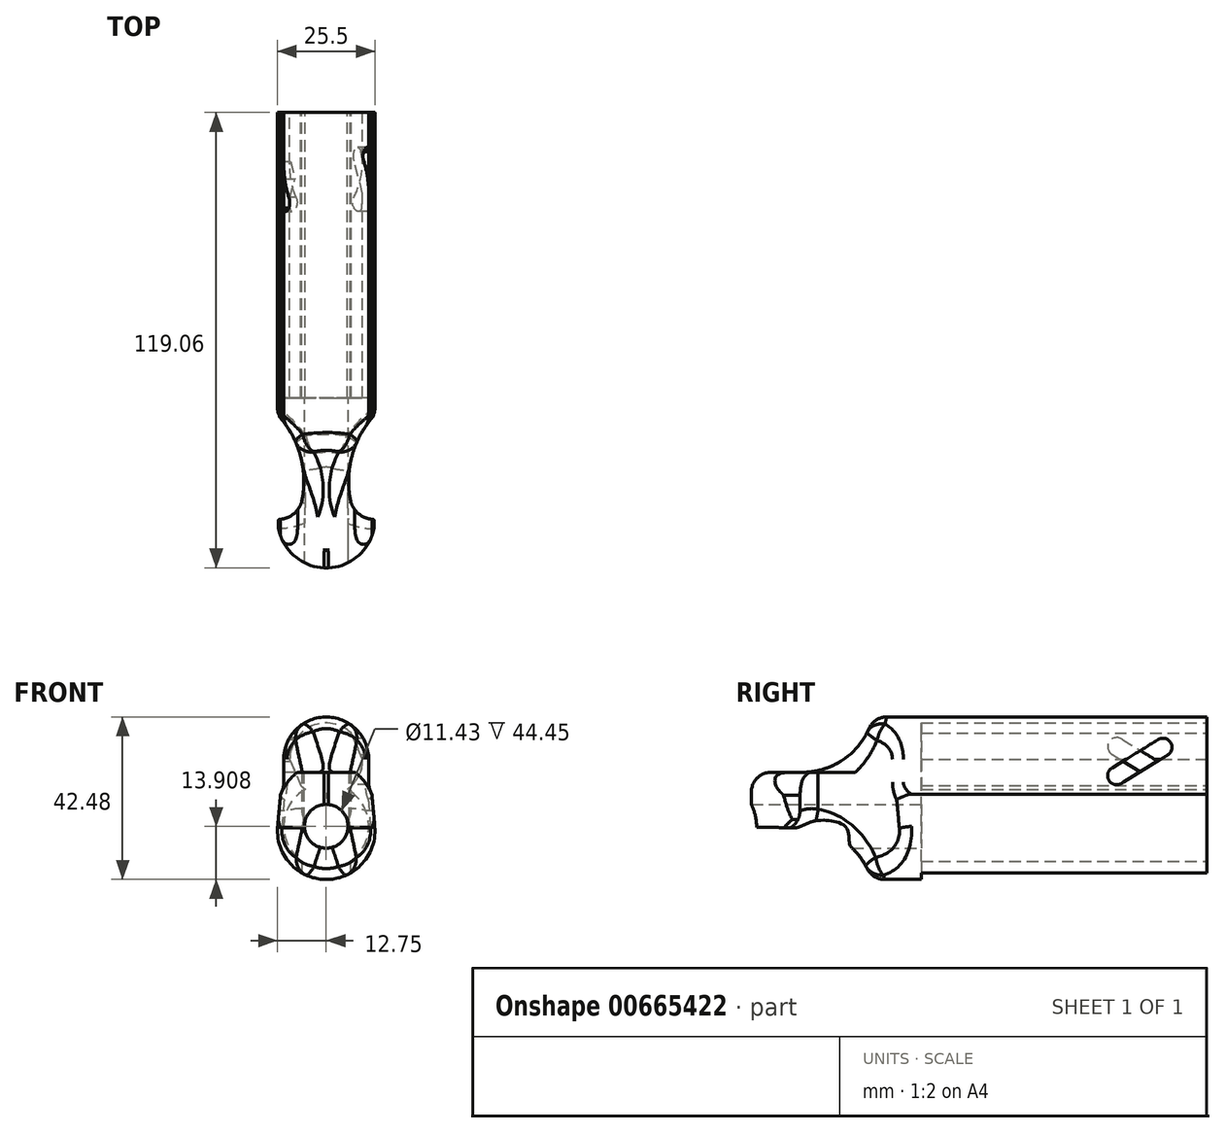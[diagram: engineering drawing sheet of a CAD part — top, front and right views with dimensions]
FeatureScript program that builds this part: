
annotation { "Feature Type Name" : "Feature", "Feature Type Description" : "" }
export const myFeature = defineFeature(function(context is Context, id is Id, definition is map)
    precondition{}
    {
        {
            var Q0;
            Q0=qCreatedBy(makeId("Front.planeOp"),FACE);
            var sketch = newSketch(context, id + "F0", { "sketchPlane" : qUnion([Q0])});
            skArc(sketch, "E0", {"start": v(5.48, -7.8) * mm, "mid": v(0, 9.53) * mm, "end": v(-5.48, -7.8) * mm});
            skArc(sketch, "E1", {"start": v(-5.48, -7.8) * mm, "mid": v(0, -28.58) * mm, "end": v(5.48, -7.8) * mm});
            skArc(sketch, "E2", {"start": v(11.11, 0) * mm, "mid": v(0, 11.11) * mm, "end": v(-11.11, 0) * mm});
            skLineSegment(sketch, "E3", {"start": v(11.11, 0) * mm, "end": v(12.7, -17.46) * mm});
            skLineSegment(sketch, "E4", {"start": v(-11.11, 0) * mm, "end": v(-12.7, -17.46) * mm});
            skLineSegment(sketch, "E5", {"start": v(17.46, -12.3) * mm, "end": v(37.37, -12.3) * mm});
            skLineSegment(sketch, "E6", {"start": v(11.11, 24.47) * mm, "end": v(37.37, -12.3) * mm});
            skLineSegment(sketch, "E7", {"start": v(11.11, -5.95) * mm, "end": v(11.11, 24.47) * mm});
            skPoint(sketch, "E8.visualSharp", {"position": v(11.11, -12.3) * mm});
            skArc(sketch, "E8.filletArc", {"start": v(11.11, -5.95) * mm, "mid": v(12.97, -10.44) * mm, "end": v(17.46, -12.3) * mm});
            skLineSegment(sketch, "E9.MirrorCS", {"start": v(-11.11, 24.47) * mm, "end": v(-37.37, -12.3) * mm});
            skLineSegment(sketch, "E10.MirrorCS", {"start": v(-11.11, -5.95) * mm, "end": v(-11.11, 24.47) * mm});
            skArc(sketch, "E11.MirrorCS", {"start": v(-11.11, -5.95) * mm, "mid": v(-12.97, -10.44) * mm, "end": v(-17.46, -12.3) * mm});
            skLineSegment(sketch, "E12.MirrorCS", {"start": v(-17.46, -12.3) * mm, "end": v(-37.37, -12.3) * mm});
            skArc(sketch, "E13", {"start": v(-12.7, -17.46) * mm, "mid": v(0, -31.37) * mm, "end": v(12.7, -17.46) * mm});
            skSolve(sketch);
        }
        {
            var Q0;
            {var subQ0=sQuery(id+"F0.wireOp",EDGE,"E0");Q0=makeQuery(id+"F0.imprint","IMPRINT",FACE,{"disambiguationData":[TD([[makeQuery(id+"F0.imprint","IMPRINT",EDGE,{"derivedFrom":subQ0}),-1.0]])]});}
            extrude(context, id + "F1", {"entities" : qUnion([Q0]), "depth" : 74.61 * mm, "offsetDistance" : 25.4 * mm});
        }
        {
            var Q0;
            Q0=makeQuery(id+"F1.opExtrude","CAP_FACE",FACE,{"disambiguationData":[OSD([sQuery(id+"F0.wireOp",EDGE,"E0"),sQuery(id+"F0.wireOp",EDGE,"E1"),sQuery(id+"F0.wireOp",EDGE,"i93pHt0q-3cz8-Kv8p-NXo6-p6uIZiVqrdmw"),sQuery(id+"F0.wireOp",EDGE,"D1jruoxV-a4U2-s1l0-eM7a-wT1BJkcVVtK3"),sQuery(id+"F0.wireOp",EDGE,"qe1SkhRB-ESz2-ejrM-H6ui-Tdr1pgu2zREs"),sQuery(id+"F0.wireOp",EDGE,"50cb2b35-ebb8-4a2a-ac11-31013a324220.filletArc"),sQuery(id+"F0.wireOp",EDGE,"ced6b576-02da-43b8-b345-90776f59c21b.filletArc"),sQuery(id+"F0.wireOp",EDGE,"7c9acb4f-49cb-4d03-afd4-daee15c41fa80.MirrorCS"),sQuery(id+"F0.wireOp",EDGE,"7c9acb4f-49cb-4d03-afd4-daee15c41fa81.MirrorCS"),sQuery(id+"F0.wireOp",EDGE,"7c9acb4f-49cb-4d03-afd4-daee15c41fa82.MirrorCS"),sQuery(id+"F0.wireOp",EDGE,"7c9acb4f-49cb-4d03-afd4-daee15c41fa83.MirrorCS"),sQuery(id+"F0.wireOp",EDGE,"7c9acb4f-49cb-4d03-afd4-daee15c41fa84.MirrorCS")])],"isStart":false});
            var sketch = newSketch(context, id + "F2", { "sketchPlane" : qUnion([Q0])});
            skArc(sketch, "E14", {"start": v(11.11, -5.95) * mm, "mid": v(11.32, -7.57) * mm, "end": v(11.94, -9.08) * mm});
            skArc(sketch, "E15", {"start": v(-11.94, -9.08) * mm, "mid": v(-11.32, -7.57) * mm, "end": v(-11.11, -5.95) * mm});
            skArc(sketch, "E16", {"start": v(-12.7, -17.46) * mm, "mid": v(0, -31.37) * mm, "end": v(12.7, -17.46) * mm});
            skArc(sketch, "E17", {"start": v(11.11, 0) * mm, "mid": v(0, 11.11) * mm, "end": v(-11.11, 0) * mm});
            skLineSegment(sketch, "E18", {"start": v(-11.11, 0) * mm, "end": v(-11.11, -5.95) * mm});
            skLineSegment(sketch, "E19", {"start": v(11.11, 0) * mm, "end": v(11.11, -5.95) * mm});
            skLineSegment(sketch, "E20", {"start": v(11.94, -9.08) * mm, "end": v(12.7, -17.46) * mm});
            skLineSegment(sketch, "E21", {"start": v(-11.94, -9.08) * mm, "end": v(-12.7, -17.46) * mm});
            skSolve(sketch);
        }
        {
            var Q0;
            Q0=qCreatedBy(makeId("Front.planeOp"),FACE);
            var sketch = newSketch(context, id + "F3", { "sketchPlane" : qUnion([Q0])});
            skLineSegment(sketch, "E22.bottom", {"start": v(-6.35, -36.2) * mm, "end": v(6.35, -36.2) * mm});
            skLineSegment(sketch, "E22.top", {"start": v(-6.35, -26.33) * mm, "end": v(6.35, -26.33) * mm});
            skLineSegment(sketch, "E22.left", {"start": v(-6.35, -36.2) * mm, "end": v(-6.35, -26.33) * mm});
            skLineSegment(sketch, "E22.right", {"start": v(6.35, -36.2) * mm, "end": v(6.35, -26.33) * mm});
            skPoint(sketch, "E22.middle", {"position": v(0, -31.27) * mm});
            skSolve(sketch);
        }
        {
            var Q0;
            Q0=makeQuery(id+"F3.imprint","IMPRINT",FACE,{"disambiguationData":[TD([[makeQuery(id+"F3.imprint","IMPRINT",EDGE,{"derivedFrom":sQuery(id+"F3.wireOp",EDGE,"E22.bottom")}),1.0]])]});
            extrude(context, id + "F4", {"entities" : qUnion([Q0]), "operationType" : NewBodyOperationType.REMOVE, "depth" : 75.44 * mm, "offsetDistance" : 25.4 * mm});
        }
        {
            var Q0;
            Q0 = qSketchRegion(id + "F2", true);
            extrude(context, id + "F5", {"entities" : qUnion([Q0]), "operationType" : NewBodyOperationType.ADD, "depth" : 6.35 * mm, "offsetDistance" : 25.4 * mm});
        }
        {
            var Q0;
            Q0=makeQuery(id+"F5.opExtrude","CAP_FACE",FACE,{"disambiguationData":[OSD([sQuery(id+"F2.wireOp",EDGE,"E14"),sQuery(id+"F2.wireOp",EDGE,"E15"),sQuery(id+"F2.wireOp",EDGE,"E16"),sQuery(id+"F2.wireOp",EDGE,"E17"),sQuery(id+"F2.wireOp",EDGE,"E18"),sQuery(id+"F2.wireOp",EDGE,"E19"),sQuery(id+"F2.wireOp",EDGE,"E20"),sQuery(id+"F2.wireOp",EDGE,"E21")])],"isStart":false});
            cPlane(context, id + "F6", {"entities" : qUnion([Q0]), "cplaneType" : CPlaneType.OFFSET, "offset" : 0 * mm, "width" : 152.4 * mm, "height" : 152.4 * mm});
        }
        {
            var Q0;
            Q0=qCreatedBy(id+"F6.planeOp",FACE);
            var sketch = newSketch(context, id + "F7", { "sketchPlane" : qUnion([Q0])});
            skArc(sketch, "E23", {"start": v(11.11, 0) * mm, "mid": v(0, 11.11) * mm, "end": v(-11.11, 0) * mm});
            skSolve(sketch);
        }
        {
            var Q0;
            Q0=qCreatedBy(id+"F6.planeOp",FACE);
            var sketch = newSketch(context, id + "F8", { "sketchPlane" : qUnion([Q0])});
            skArc(sketch, "E24", {"start": v(-12.7, -17.46) * mm, "mid": v(0, -31.37) * mm, "end": v(12.7, -17.46) * mm});
            skLineSegment(sketch, "E25", {"start": v(-11.11, 0) * mm, "end": v(-11.11, -5.95) * mm});
            skLineSegment(sketch, "E26", {"start": v(11.11, 0) * mm, "end": v(11.11, -5.95) * mm});
            skArc(sketch, "E27", {"start": v(11.11, -5.95) * mm, "mid": v(11.32, -7.57) * mm, "end": v(11.94, -9.08) * mm});
            skLineSegment(sketch, "E28", {"start": v(11.94, -9.08) * mm, "end": v(12.7, -17.46) * mm});
            skArc(sketch, "E29", {"start": v(-11.94, -9.08) * mm, "mid": v(-11.32, -7.57) * mm, "end": v(-11.11, -5.95) * mm});
            skLineSegment(sketch, "E30", {"start": v(-11.94, -9.08) * mm, "end": v(-12.7, -17.46) * mm});
            skArc(sketch, "E31", {"start": v(11.11, 0) * mm, "mid": v(0, 11.11) * mm, "end": v(-11.11, 0) * mm});
            skSolve(sketch);
        }
        {
            var Q0;
            Q0 = qSketchRegion(id + "F8", true);
            extrude(context, id + "F9", {"entities" : qUnion([Q0]), "operationType" : NewBodyOperationType.ADD, "depth" : 38.1 * mm, "offsetDistance" : 25.4 * mm});
        }
        {
            var Q0;
            Q0=makeQuery(id+"F5.opExtrude","CAP_FACE",FACE,{"disambiguationData":[OSD([sQuery(id+"F2.wireOp",EDGE,"E14"),sQuery(id+"F2.wireOp",EDGE,"E15"),sQuery(id+"F2.wireOp",EDGE,"E16"),sQuery(id+"F2.wireOp",EDGE,"E17"),sQuery(id+"F2.wireOp",EDGE,"E18"),sQuery(id+"F2.wireOp",EDGE,"E19"),sQuery(id+"F2.wireOp",EDGE,"E20"),sQuery(id+"F2.wireOp",EDGE,"E21")])],"isStart":true});
            var sketch = newSketch(context, id + "F10", { "sketchPlane" : qUnion([Q0])});
            skCircle(sketch, "E32", {"center": v(0, -17.46) * mm, "radius": 5.72 * mm});
            skSolve(sketch);
        }
        {
            var Q0;
            Q0 = qSketchRegion(id + "F10", true);
            extrude(context, id + "F11", {"entities" : qUnion([Q0]), "operationType" : NewBodyOperationType.REMOVE, "oppositeDirection" : true, "depth" : 50.8 * mm, "offsetDistance" : 25.4 * mm});
        }
        {
            var Q0;
            Q0=qCreatedBy(makeId("Right.planeOp"),FACE);
            var sketch = newSketch(context, id + "F12", { "sketchPlane" : qUnion([Q0])});
            skArc(sketch, "E33", {"start": v(-105.86, -3.35) * mm, "mid": v(-93.15, 29.94) * mm, "end": v(-124.71, 13.4) * mm});
            skLineSegment(sketch, "E34", {"start": v(-80.96, 11.11) * mm, "end": v(-87.31, 11.11) * mm});
            skLineSegment(sketch, "E35", {"start": v(-105.74, -3.35) * mm, "end": v(-124.71, -3.35) * mm});
            skLineSegment(sketch, "E36", {"start": v(-124.71, -3.35) * mm, "end": v(-124.71, 13.4) * mm});
            skArc(sketch, "E37", {"start": v(-124.87, -35.72) * mm, "mid": v(-92.98, -51) * mm, "end": v(-105.49, -17.92) * mm});
            skLineSegment(sketch, "E38", {"start": v(-105.49, -17.92) * mm, "end": v(-125.74, -17.52) * mm});
            skLineSegment(sketch, "E39", {"start": v(-125.74, -17.52) * mm, "end": v(-124.67, -40.01) * mm});
            skSolve(sketch);
        }
        {
            var Q0;
            {var subQ4=sQuery(id+"F12.wireOp",EDGE,"E36");Q0=makeQuery(id+"F12.imprint","IMPRINT",FACE,{"disambiguationData":[TD([[makeQuery(id+"F12.imprint","IMPRINT",EDGE,{"derivedFrom":subQ4}),-1.0]])]});}
            var Q1;
            {var subQ0=sQuery(id+"F12.wireOp",EDGE,"E38");Q1=makeQuery(id+"F12.imprint","IMPRINT",FACE,{"disambiguationData":[TD([[makeQuery(id+"F12.imprint","IMPRINT",EDGE,{"derivedFrom":subQ0}),1.0]])]});}
            extrude(context, id + "F13", {"entities" : qUnion([Q0, Q1]), "operationType" : NewBodyOperationType.REMOVE, "depth" : 31.75 * mm, "offsetDistance" : 25.4 * mm, "symmetric" : true});
        }
        {
            var Q0;
            Q0=qCreatedBy(makeId("Top.planeOp"),FACE);
            var sketch = newSketch(context, id + "F14", { "sketchPlane" : qUnion([Q0])});
            skPoint(sketch, "E40.end.orphan", {"position": v(12.7, -106.38) * mm});
            skArc(sketch, "E41", {"start": v(6.23, -100.8) * mm, "mid": v(8.39, -104.84) * mm, "end": v(12.7, -106.38) * mm});
            skArc(sketch, "E42", {"start": v(11.11, -80.96) * mm, "mid": v(6.59, -90.37) * mm, "end": v(6.23, -100.8) * mm});
            skArc(sketch, "E43.MirrorCS", {"start": v(-6.23, -100.8) * mm, "mid": v(-8.39, -104.84) * mm, "end": v(-12.7, -106.38) * mm});
            skArc(sketch, "E44.MirrorCS", {"start": v(-11.11, -80.96) * mm, "mid": v(-6.59, -90.37) * mm, "end": v(-6.23, -100.8) * mm});
            skArc(sketch, "E45.trimOffspring", {"start": v(-12.7, -106.38) * mm, "mid": v(0, -119.08) * mm, "end": v(12.7, -106.38) * mm});
            skArc(sketch, "E46", {"start": v(31.25, -121.84) * mm, "mid": v(47.27, -76.73) * mm, "end": v(6.39, -101.64) * mm});
            skArc(sketch, "E47", {"start": v(-6.39, -101.64) * mm, "mid": v(-47.27, -76.73) * mm, "end": v(-31.25, -121.84) * mm});
            skLineSegment(sketch, "E48", {"start": v(-31.25, -121.84) * mm, "end": v(31.25, -121.84) * mm});
            skSolve(sketch);
        }
        {
            var Q0;
            {var subQ4=sQuery(id+"F14.wireOp",EDGE,"E45.trimOffspring");Q0=makeQuery(id+"F14.imprint","IMPRINT",FACE,{"disambiguationData":[TD([[makeQuery(id+"F14.imprint","IMPRINT",EDGE,{"derivedFrom":subQ4}),-1.0]])]});}
            extrude(context, id + "F15", {"entities" : qUnion([Q0]), "operationType" : NewBodyOperationType.REMOVE, "depth" : 76.2 * mm, "offsetDistance" : 25.4 * mm, "symmetric" : true});
        }
        {
            var Q0;
            Q0=qCreatedBy(id+"F6.planeOp",FACE);
            cPlane(context, id + "F16", {"entities" : qUnion([Q0]), "cplaneType" : CPlaneType.OFFSET, "offset" : 25.4 * mm, "width" : 152.4 * mm, "height" : 152.4 * mm});
        }
        {
            var Q0;
            Q0=qCreatedBy(id+"F16.planeOp",FACE);
            var sketch = newSketch(context, id + "F17", { "sketchPlane" : qUnion([Q0])});
            skCircle(sketch, "E49", {"center": v(0, -13.61) * mm, "radius": 12.7 * mm});
            skLineSegment(sketch, "E50.bottom", {"start": v(14.5, -27.58) * mm, "end": v(-14.5, -27.58) * mm});
            skLineSegment(sketch, "E50.top", {"start": v(14.5, 0.36) * mm, "end": v(-14.5, 0.36) * mm});
            skLineSegment(sketch, "E50.left", {"start": v(14.5, -27.58) * mm, "end": v(14.5, 0.36) * mm});
            skLineSegment(sketch, "E50.right", {"start": v(-14.5, -27.58) * mm, "end": v(-14.5, 0.36) * mm});
            skSolve(sketch);
        }
        {
            var Q0;
            Q0=makeQuery(id+"F17.imprint","IMPRINT",FACE,{"disambiguationData":[TD([[makeQuery(id+"F17.imprint","IMPRINT",EDGE,{"derivedFrom":sQuery(id+"F17.wireOp",EDGE,"E49")}),-1.0]])]});
            extrude(context, id + "F18", {"entities" : qUnion([Q0]), "operationType" : NewBodyOperationType.REMOVE, "oppositeDirection" : true, "depth" : 5.08 * mm, "offsetDistance" : 25.4 * mm, "hasSecondDirection" : true, "secondDirectionOppositeDirection" : false, "secondDirectionDepth" : 25.4 * mm});
        }
        {
            var Q0;
            Q0=makeQuery(id+"F15.boolean.opBoolean","INTERSECT",EDGE,{"derivedFrom":[makeQuery(id+"F9.boolean.opBoolean","MERGE",FACE,{"derivedFrom":[makeQuery(id+"F5.boolean.opBoolean","MERGE",FACE,{"derivedFrom":[makeQuery(id+"F1.opExtrude","SWEPT_FACE",FACE,{"disambiguationData":[OSD([sQuery(id+"F0.wireOp",EDGE,"E2")])]}),makeQuery(id+"F5.opExtrude","SWEPT_FACE",FACE,{"disambiguationData":[OSD([sQuery(id+"F2.wireOp",EDGE,"E17")])]})]}),makeQuery(id+"F9.opExtrude","SWEPT_FACE",FACE,{"disambiguationData":[OSD([sQuery(id+"F8.wireOp",EDGE,"E31")])]})]}),makeQuery(id+"F15.opExtrude","SWEPT_FACE",FACE,{"disambiguationData":[OSD([sQuery(id+"F14.wireOp",EDGE,"E47")])]})]});
            var Q1;
            Q1=makeQuery(id+"F15.boolean.opBoolean","INTERSECT",EDGE,{"derivedFrom":[makeQuery(id+"F9.boolean.opBoolean","MERGE",FACE,{"derivedFrom":[makeQuery(id+"F5.boolean.opBoolean","MERGE",FACE,{"derivedFrom":[makeQuery(id+"F1.opExtrude","SWEPT_FACE",FACE,{"disambiguationData":[OSD([sQuery(id+"F0.wireOp",EDGE,"E4")])]}),makeQuery(id+"F5.opExtrude","SWEPT_FACE",FACE,{"disambiguationData":[OSD([sQuery(id+"F2.wireOp",EDGE,"E21")])]})]}),makeQuery(id+"F9.opExtrude","SWEPT_FACE",FACE,{"disambiguationData":[OSD([sQuery(id+"F8.wireOp",EDGE,"E30")])]})]}),makeQuery(id+"F15.opExtrude","SWEPT_FACE",FACE,{"disambiguationData":[OSD([sQuery(id+"F14.wireOp",EDGE,"E47")])]})]});
            var Q2;
            Q2=makeQuery(id+"F15.boolean.opBoolean","INTERSECT",EDGE,{"derivedFrom":[makeQuery(id+"F13.boolean.opBoolean","COPY",FACE,{"derivedFrom":makeQuery(id+"F13.opExtrude","SWEPT_FACE",FACE,{"disambiguationData":[OSD([sQuery(id+"F12.wireOp",EDGE,"E37")])]})}),makeQuery(id+"F15.opExtrude","SWEPT_FACE",FACE,{"disambiguationData":[OSD([sQuery(id+"F14.wireOp",EDGE,"E47")])]})]});
            var Q3;
            Q3=makeQuery(id+"F15.boolean.opBoolean","INTERSECT",EDGE,{"derivedFrom":[makeQuery(id+"F13.boolean.opBoolean","COPY",FACE,{"derivedFrom":makeQuery(id+"F13.opExtrude","SWEPT_FACE",FACE,{"disambiguationData":[OSD([sQuery(id+"F12.wireOp",EDGE,"E33")])]})}),makeQuery(id+"F15.opExtrude","SWEPT_FACE",FACE,{"disambiguationData":[OSD([sQuery(id+"F14.wireOp",EDGE,"E47")])]})]});
            var Q4;
            Q4=makeQuery(id+"F15.boolean.opBoolean","INTERSECT",EDGE,{"derivedFrom":[makeQuery(id+"F9.boolean.opBoolean","MERGE",FACE,{"derivedFrom":[makeQuery(id+"F5.boolean.opBoolean","MERGE",FACE,{"derivedFrom":[makeQuery(id+"F1.opExtrude","SWEPT_FACE",FACE,{"disambiguationData":[OSD([sQuery(id+"F0.wireOp",EDGE,"E2")])]}),makeQuery(id+"F5.opExtrude","SWEPT_FACE",FACE,{"disambiguationData":[OSD([sQuery(id+"F2.wireOp",EDGE,"E17")])]})]}),makeQuery(id+"F9.opExtrude","SWEPT_FACE",FACE,{"disambiguationData":[OSD([sQuery(id+"F8.wireOp",EDGE,"E31")])]})]}),makeQuery(id+"F15.opExtrude","SWEPT_FACE",FACE,{"disambiguationData":[OSD([sQuery(id+"F14.wireOp",EDGE,"E46")])]})]});
            var Q5;
            Q5=makeQuery(id+"F15.boolean.opBoolean","INTERSECT",EDGE,{"derivedFrom":[makeQuery(id+"F13.boolean.opBoolean","COPY",FACE,{"derivedFrom":makeQuery(id+"F13.opExtrude","SWEPT_FACE",FACE,{"disambiguationData":[OSD([sQuery(id+"F12.wireOp",EDGE,"E33")])]})}),makeQuery(id+"F15.opExtrude","SWEPT_FACE",FACE,{"disambiguationData":[OSD([sQuery(id+"F14.wireOp",EDGE,"E46")])]})]});
            var Q6;
            Q6=makeQuery(id+"F15.boolean.opBoolean","INTERSECT",EDGE,{"derivedFrom":[makeQuery(id+"F9.boolean.opBoolean","MERGE",FACE,{"derivedFrom":[makeQuery(id+"F5.boolean.opBoolean","MERGE",FACE,{"derivedFrom":[makeQuery(id+"F1.opExtrude","SWEPT_FACE",FACE,{"disambiguationData":[OSD([sQuery(id+"F0.wireOp",EDGE,"E3")])]}),makeQuery(id+"F5.opExtrude","SWEPT_FACE",FACE,{"disambiguationData":[OSD([sQuery(id+"F2.wireOp",EDGE,"E20")])]})]}),makeQuery(id+"F9.opExtrude","SWEPT_FACE",FACE,{"disambiguationData":[OSD([sQuery(id+"F8.wireOp",EDGE,"E28")])]})]}),makeQuery(id+"F15.opExtrude","SWEPT_FACE",FACE,{"disambiguationData":[OSD([sQuery(id+"F14.wireOp",EDGE,"E46")])]})]});
            var Q7;
            Q7=makeQuery(id+"F15.boolean.opBoolean","INTERSECT",EDGE,{"derivedFrom":[makeQuery(id+"F13.boolean.opBoolean","COPY",FACE,{"derivedFrom":makeQuery(id+"F13.opExtrude","SWEPT_FACE",FACE,{"disambiguationData":[OSD([sQuery(id+"F12.wireOp",EDGE,"E37")])]})}),makeQuery(id+"F15.opExtrude","SWEPT_FACE",FACE,{"disambiguationData":[OSD([sQuery(id+"F14.wireOp",EDGE,"E46")])]})]});
            var Q8;
            Q8=makeQuery(id+"F13.boolean.opBoolean","INTERSECT",EDGE,{"derivedFrom":[makeQuery(id+"F9.boolean.opBoolean","MERGE",FACE,{"derivedFrom":[makeQuery(id+"F5.boolean.opBoolean","MERGE",FACE,{"derivedFrom":[makeQuery(id+"F1.opExtrude","SWEPT_FACE",FACE,{"disambiguationData":[OSD([sQuery(id+"F0.wireOp",EDGE,"E2")])]}),makeQuery(id+"F5.opExtrude","SWEPT_FACE",FACE,{"disambiguationData":[OSD([sQuery(id+"F2.wireOp",EDGE,"E17")])]})]}),makeQuery(id+"F9.opExtrude","SWEPT_FACE",FACE,{"disambiguationData":[OSD([sQuery(id+"F8.wireOp",EDGE,"E31")])]})]}),makeQuery(id+"F13.opExtrude","SWEPT_FACE",FACE,{"disambiguationData":[OSD([sQuery(id+"F12.wireOp",EDGE,"E33")])]})]});
            var Q9;
            {var subQ0=sQuery(id+"F0.wireOp",EDGE,"E13");var subQ5=sQuery(id+"F0.wireOp",EDGE,"E4");var subQ6=sQuery(id+"F0.wireOp",EDGE,"E3");var subQ12=makeQuery(id+"F1.opExtrude","SWEPT_FACE",FACE,{"disambiguationData":[OSD([subQ0])]});Q9=makeQuery(id+"F13.boolean.opBoolean","INTERSECT",EDGE,{"derivedFrom":[makeQuery(id+"F9.boolean.opBoolean","MERGE",FACE,{"derivedFrom":[makeQuery(id+"F5.boolean.opBoolean","MERGE",FACE,{"derivedFrom":[makeQuery(id+"F4.boolean.opBoolean","SPLIT",FACE,{"disambiguationData":[TD([makeQuery(id+"F1.opExtrude","SWEPT_FACE",FACE,{"disambiguationData":[OSD([subQ6])]})])],"derivedFrom":subQ12}),makeQuery(id+"F4.boolean.opBoolean","SPLIT",FACE,{"disambiguationData":[TD([makeQuery(id+"F1.opExtrude","SWEPT_FACE",FACE,{"disambiguationData":[OSD([subQ5])]})])],"derivedFrom":subQ12}),makeQuery(id+"F5.opExtrude","SWEPT_FACE",FACE,{"disambiguationData":[OSD([sQuery(id+"F2.wireOp",EDGE,"E16")])]})]}),makeQuery(id+"F9.opExtrude","SWEPT_FACE",FACE,{"disambiguationData":[OSD([sQuery(id+"F8.wireOp",EDGE,"E24")])]})]}),makeQuery(id+"F13.opExtrude","SWEPT_FACE",FACE,{"disambiguationData":[OSD([sQuery(id+"F12.wireOp",EDGE,"E37")])]})]});}
            var Q10;
            Q10=makeQuery(id+"F15.boolean.opBoolean","INTERSECT",EDGE,{"disambiguationData":[OD(1.0)],"derivedFrom":[makeQuery(id+"F13.boolean.opBoolean","COPY",FACE,{"derivedFrom":makeQuery(id+"F13.opExtrude","SWEPT_FACE",FACE,{"disambiguationData":[OSD([sQuery(id+"F12.wireOp",EDGE,"E35")])]})}),makeQuery(id+"F15.opExtrude","SWEPT_FACE",FACE,{"disambiguationData":[OSD([sQuery(id+"F14.wireOp",EDGE,"E45.trimOffspring")])]})]});
            fillet(context, id + "F19", {"entities" : qUnion([Q0, Q1, Q2, Q3, Q4, Q5, Q6, Q7, Q8, Q9, Q10]), "radius" : 5.08 * mm, "tangentPropagation" : true, "allowEdgeOverflow" : false});
        }
        {
            var Q0;
            Q0=qCreatedBy(makeId("Front.planeOp"),FACE);
            var sketch = newSketch(context, id + "F20", { "sketchPlane" : qUnion([Q0])});
            skArc(sketch, "E51.trimOffspring", {"start": v(-5.29, 7.92) * mm, "mid": v(-5.3, 7.92) * mm, "end": v(-5.3, 7.91) * mm});
            skLineSegment(sketch, "E52.MirrorCS", {"start": v(-9.53, 0) * mm, "end": v(-6.6, -6.86) * mm});
            skLineSegment(sketch, "E53.MirrorCS", {"start": v(9.53, 0) * mm, "end": v(6.6, 6.86) * mm});
            skPoint(sketch, "E54.MirrorCS.start.orphan", {"position": v(9.53, 0) * mm});
            skPoint(sketch, "E55.start.orphan", {"position": v(-9.53, 0) * mm});
            skArc(sketch, "E56.trimOffspring", {"start": v(-9.52, 0) * mm, "mid": v(-8.77, -3.73) * mm, "end": v(-6.6, -6.86) * mm});
            skArc(sketch, "E57.trimOffspring", {"start": v(9.52, 0) * mm, "mid": v(8.77, 3.73) * mm, "end": v(6.6, 6.86) * mm});
            skSolve(sketch);
        }
        {
            var Q0;
            Q0 = qSketchRegion(id + "F20", true);
            extrude(context, id + "F21", {"entities" : qUnion([Q0]), "operationType" : NewBodyOperationType.ADD, "depth" : 74.61 * mm, "offsetDistance" : 25.4 * mm});
        }
        {
            var Q0;
            Q0=qCreatedBy(makeId("Right.planeOp"),FACE);
            var sketch = newSketch(context, id + "F22", { "sketchPlane" : qUnion([Q0])});
            skArc(sketch, "E58", {"start": v(-10.22, 1.17) * mm, "mid": v(-9.16, 4.58) * mm, "end": v(-12.67, 5.21) * mm});
            skArc(sketch, "E59", {"start": v(-24.77, -2.2) * mm, "mid": v(-25.55, -5.48) * mm, "end": v(-22.28, -6.26) * mm});
            skLineSegment(sketch, "E60", {"start": v(-12.67, 5.21) * mm, "end": v(-24.77, -2.2) * mm});
            skLineSegment(sketch, "E61", {"start": v(-9.7, 1.5) * mm, "end": v(-22.28, -6.26) * mm});
            skLineSegment(sketch, "E62.MirrorCS", {"start": v(-22.05, 5.21) * mm, "end": v(-9.95, -2.2) * mm});
            skArc(sketch, "E63.MirrorCS", {"start": v(-9.95, -2.2) * mm, "mid": v(-9.17, -5.48) * mm, "end": v(-12.44, -6.26) * mm});
            skLineSegment(sketch, "E64.MirrorCS", {"start": v(-25.02, 1.5) * mm, "end": v(-12.44, -6.26) * mm});
            skArc(sketch, "E65.MirrorCS", {"start": v(-24.5, 1.17) * mm, "mid": v(-25.56, 4.58) * mm, "end": v(-22.05, 5.21) * mm});
            skSolve(sketch);
        }
        {
            var Q0;
            {var subQ5=sQuery(id+"F22.wireOp",EDGE,"E63.MirrorCS");Q0=makeQuery(id+"F22.imprint","IMPRINT",FACE,{"disambiguationData":[TD([[makeQuery(id+"F22.imprint","IMPRINT",EDGE,{"derivedFrom":subQ5}),-1.0]])]});}
            var Q1;
            {var subQ0=sQuery(id+"F22.wireOp",EDGE,"E62.MirrorCS");var subQ1=sQuery(id+"F22.wireOp",EDGE,"E60");var subQ2=makeQuery(id+"F22.imprint","INTERSECT",VERTEX,{"derivedFrom":[subQ1,subQ0]});Q1=makeQuery(id+"F22.imprint","IMPRINT",FACE,{"disambiguationData":[TD([[makeQuery(id+"F22.imprint","IMPRINT",EDGE,{"disambiguationData":[TD([[subQ2,-1.0]])],"derivedFrom":subQ1}),1.0]])]});}
            var Q2;
            {var subQ3=sQuery(id+"F22.wireOp",EDGE,"E60");var subQ5=sQuery(id+"F22.wireOp",EDGE,"E62.MirrorCS");var subQ6=makeQuery(id+"F22.imprint","INTERSECT",VERTEX,{"derivedFrom":[subQ3,subQ5]});Q2=makeQuery(id+"F22.imprint","IMPRINT",FACE,{"disambiguationData":[TD([[makeQuery(id+"F22.imprint","IMPRINT",EDGE,{"disambiguationData":[TD([[subQ6,-1.0]])],"derivedFrom":subQ3}),-1.0]])]});}
            extrude(context, id + "F23", {"entities" : qUnion([Q0, Q1, Q2]), "operationType" : NewBodyOperationType.REMOVE, "oppositeDirection" : true, "depth" : 25.4 * mm, "offsetDistance" : 25.4 * mm});
        }
        {
            var Q0;
            Q0=qCreatedBy(makeId("Right.planeOp"),FACE);
            var sketch = newSketch(context, id + "F24", { "sketchPlane" : qUnion([Q0])});
            skLineSegment(sketch, "E66", {"start": v(-24.77, -2.2) * mm, "end": v(-12.67, 5.21) * mm});
            skLineSegment(sketch, "E67", {"start": v(-22.28, -6.26) * mm, "end": v(-10.22, 1.17) * mm});
            skArc(sketch, "E68", {"start": v(-24.77, -2.2) * mm, "mid": v(-25.55, -5.48) * mm, "end": v(-22.28, -6.26) * mm});
            skArc(sketch, "E69", {"start": v(-10.22, 1.17) * mm, "mid": v(-9.41, 4.43) * mm, "end": v(-12.67, 5.21) * mm});
            skSolve(sketch);
        }
        {
            var Q0;
            Q0 = qSketchRegion(id + "F24", true);
            extrude(context, id + "F25", {"entities" : qUnion([Q0]), "operationType" : NewBodyOperationType.REMOVE, "depth" : 25.4 * mm, "offsetDistance" : 25.4 * mm});
        }
    });
